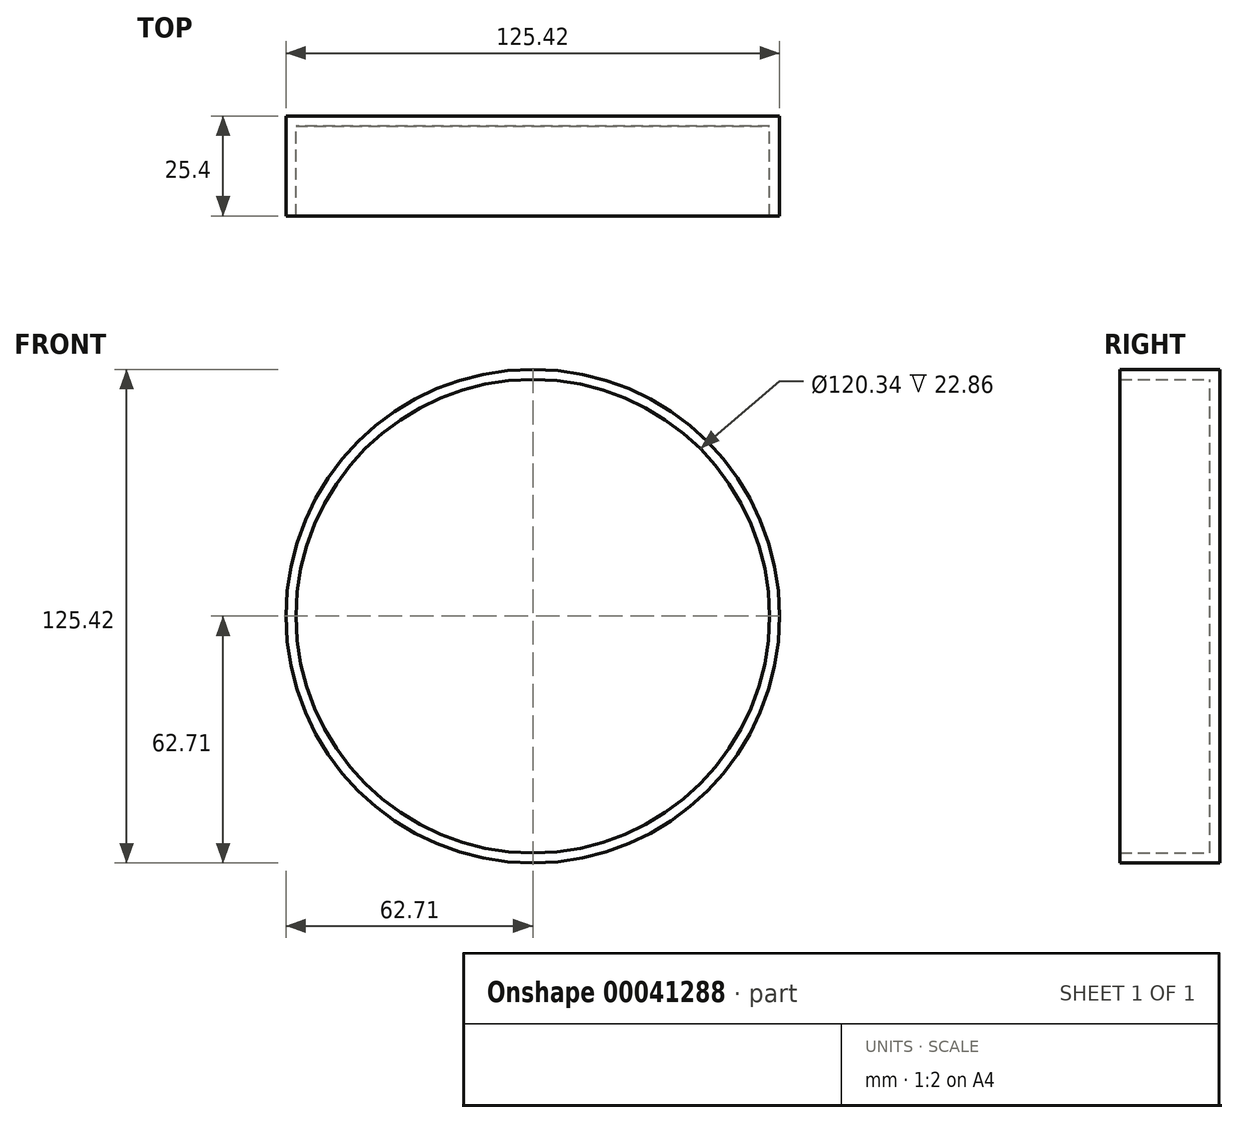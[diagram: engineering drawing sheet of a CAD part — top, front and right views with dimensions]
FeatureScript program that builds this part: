
annotation { "Feature Type Name" : "Feature", "Feature Type Description" : "" }
export const myFeature = defineFeature(function(context is Context, id is Id, definition is map)
    precondition{}
    {
        {
            var Q0;
            Q0=qCreatedBy(makeId("Front.planeOp"),FACE);
            var sketch = newSketch(context, id + "F0", { "sketchPlane" : qUnion([Q0])});
            skFitSpline(sketch, "E0", {"points": [v(-55.2, 58.15) * mm, v(-56.05, -7.43) * mm, v(45.68, 18.64) * mm, v(-13.17, 59.83) * mm, v(-33.63, 44.42) * mm, v(-55.2, 58.15) * mm]});
            skSolve(sketch);
        }
        {
            var Q0;
            Q0=makeQuery(id+"F0.imprint","IMPRINT",FACE,{"disambiguationData":[TD([[makeQuery(id+"F0.imprint","IMPRINT",EDGE,{"derivedFrom":sQuery(id+"F0.wireOp",EDGE,"E0")}),1.0]])]});
            extrude(context, id + "F1", {"entities" : qUnion([Q0]), "depth" : 25.4 * mm});
        }
        {
            var Q0;
            Q0=makeQuery(id+"F1.opExtrude","SWEPT_BODY",BODY,{"disambiguationData":[OSD([sQuery(id+"F0.wireOp",EDGE,"E0")])]});
            deleteBodies(context, id + "F2", {"entities" : qUnion([Q0])});
        }
        {
            var Q0;
            Q0=qCreatedBy(makeId("Front.planeOp"),FACE);
            var sketch = newSketch(context, id + "F3", { "sketchPlane" : qUnion([Q0])});
            skCircle(sketch, "E1", {"center": v(0, 0) * mm, "radius": 39.3 * mm});
            skSolve(sketch);
        }
        {
            var Q0;
            Q0=makeQuery(id+"F3.imprint","IMPRINT",FACE,{"disambiguationData":[TD([[makeQuery(id+"F3.imprint","IMPRINT",EDGE,{"derivedFrom":sQuery(id+"F3.wireOp",EDGE,"E1")}),1.0]])]});
            extrude(context, id + "F4", {"entities" : qUnion([Q0]), "depth" : 25.4 * mm});
        }
        {
            var Q0;
            Q0=makeQuery(id+"F4.opExtrude","SWEPT_BODY",BODY,{"disambiguationData":[OSD([sQuery(id+"F3.wireOp",EDGE,"E1")])]});
            deleteBodies(context, id + "F5", {"entities" : qUnion([Q0])});
        }
        {
            var Q0;
            Q0=qCreatedBy(makeId("Front.planeOp"),FACE);
            var sketch = newSketch(context, id + "F6", { "sketchPlane" : qUnion([Q0])});
            skCircle(sketch, "E2", {"center": v(0, 0) * mm, "radius": 62.7 * mm});
            skSolve(sketch);
        }
        {
            var Q0;
            Q0=makeQuery(id+"F6.imprint","IMPRINT",FACE,{"disambiguationData":[TD([[makeQuery(id+"F6.imprint","IMPRINT",EDGE,{"derivedFrom":sQuery(id+"F6.wireOp",EDGE,"E2")}),1.0]])]});
            extrude(context, id + "F7", {"entities" : qUnion([Q0]), "depth" : 25.4 * mm});
        }
        {
            var Q0;
            Q0=makeQuery(id+"F7.opExtrude","CAP_FACE",FACE,{"disambiguationData":[OSD([sQuery(id+"F6.wireOp",EDGE,"E2")])],"isStart":false});
            shell(context, id + "F8", {"entities" : qUnion([Q0]), "thickness" : 2.54 * mm});
        }
    });
